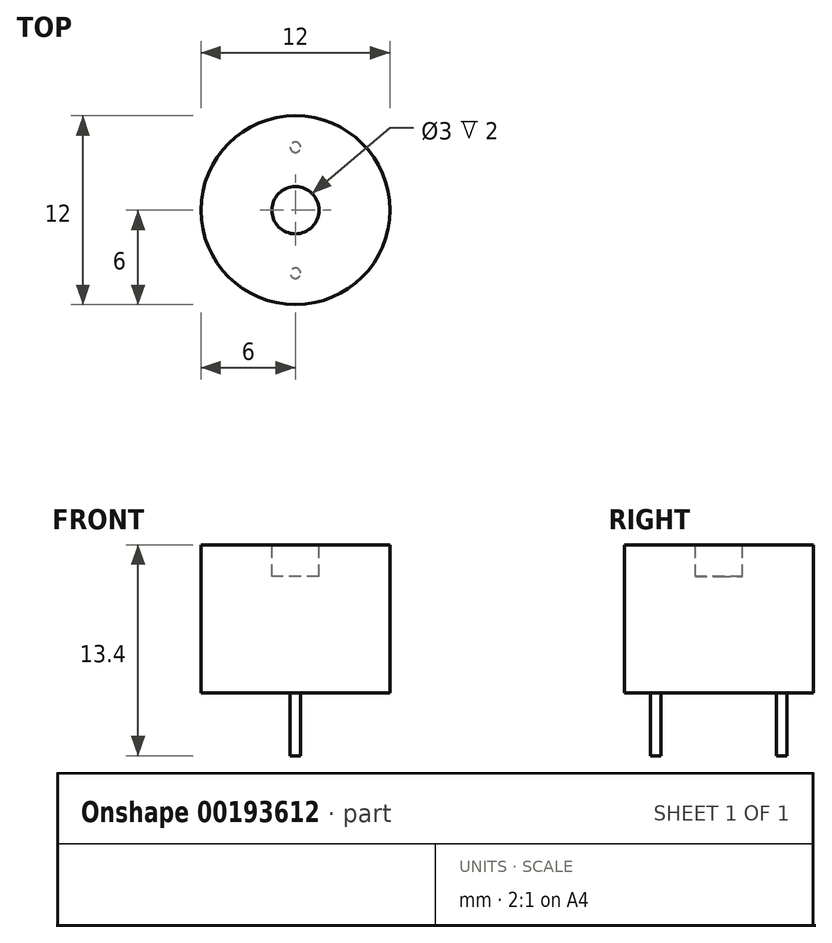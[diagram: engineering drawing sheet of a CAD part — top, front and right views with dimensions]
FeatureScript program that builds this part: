
annotation { "Feature Type Name" : "Feature", "Feature Type Description" : "" }
export const myFeature = defineFeature(function(context is Context, id is Id, definition is map)
    precondition{}
    {
        {
            var Q0;
            Q0=qCreatedBy(makeId("Top.planeOp"),FACE);
            var sketch = newSketch(context, id + "F0", { "sketchPlane" : qUnion([Q0])});
            skCircle(sketch, "E0", {"center": v(0, 0) * mm, "radius": 6 * mm});
            skSolve(sketch);
        }
        {
            var Q0;
            Q0 = qSketchRegion(id + "F0", true);
            extrude(context, id + "F1", {"entities" : qUnion([Q0]), "endBound" : BoundingType.SYMMETRIC, "depth" : 9.4 * mm, "offsetDistance" : 25 * mm});
        }
        {
            var Q0;
            Q0=makeQuery(id+"F1.opExtrude","CAP_FACE",FACE,{"disambiguationData":[OSD([sQuery(id+"F0.wireOp",EDGE,"E0")])],"isStart":false});
            var sketch = newSketch(context, id + "F2", { "sketchPlane" : qUnion([Q0])});
            skCircle(sketch, "E1", {"center": v(0, 0) * mm, "radius": 1.5 * mm});
            skSolve(sketch);
        }
        {
            var Q0;
            Q0 = qSketchRegion(id + "F2", true);
            extrude(context, id + "F3", {"entities" : qUnion([Q0]), "operationType" : NewBodyOperationType.REMOVE, "oppositeDirection" : true, "depth" : 2 * mm, "offsetDistance" : 25 * mm});
        }
        {
            var Q0;
            Q0=makeQuery(id+"F1.opExtrude","CAP_FACE",FACE,{"disambiguationData":[OSD([sQuery(id+"F0.wireOp",EDGE,"E0")])],"isStart":true});
            var sketch = newSketch(context, id + "F4", { "sketchPlane" : qUnion([Q0])});
            skLineSegment(sketch, "E2", {"start": v(0, -4) * mm, "end": v(0, 4) * mm, "construction": true});
            skPoint(sketch, "E3", {"position": v(0, 0) * mm});
            skCircle(sketch, "E4", {"center": v(0, 4) * mm, "radius": 0.33 * mm});
            skCircle(sketch, "E5", {"center": v(0, -4) * mm, "radius": 0.33 * mm});
            skSolve(sketch);
        }
        {
            var Q0;
            Q0 = qSketchRegion(id + "F4", true);
            extrude(context, id + "F5", {"entities" : qUnion([Q0]), "operationType" : NewBodyOperationType.ADD, "depth" : 4 * mm, "offsetDistance" : 25 * mm});
        }
    });
